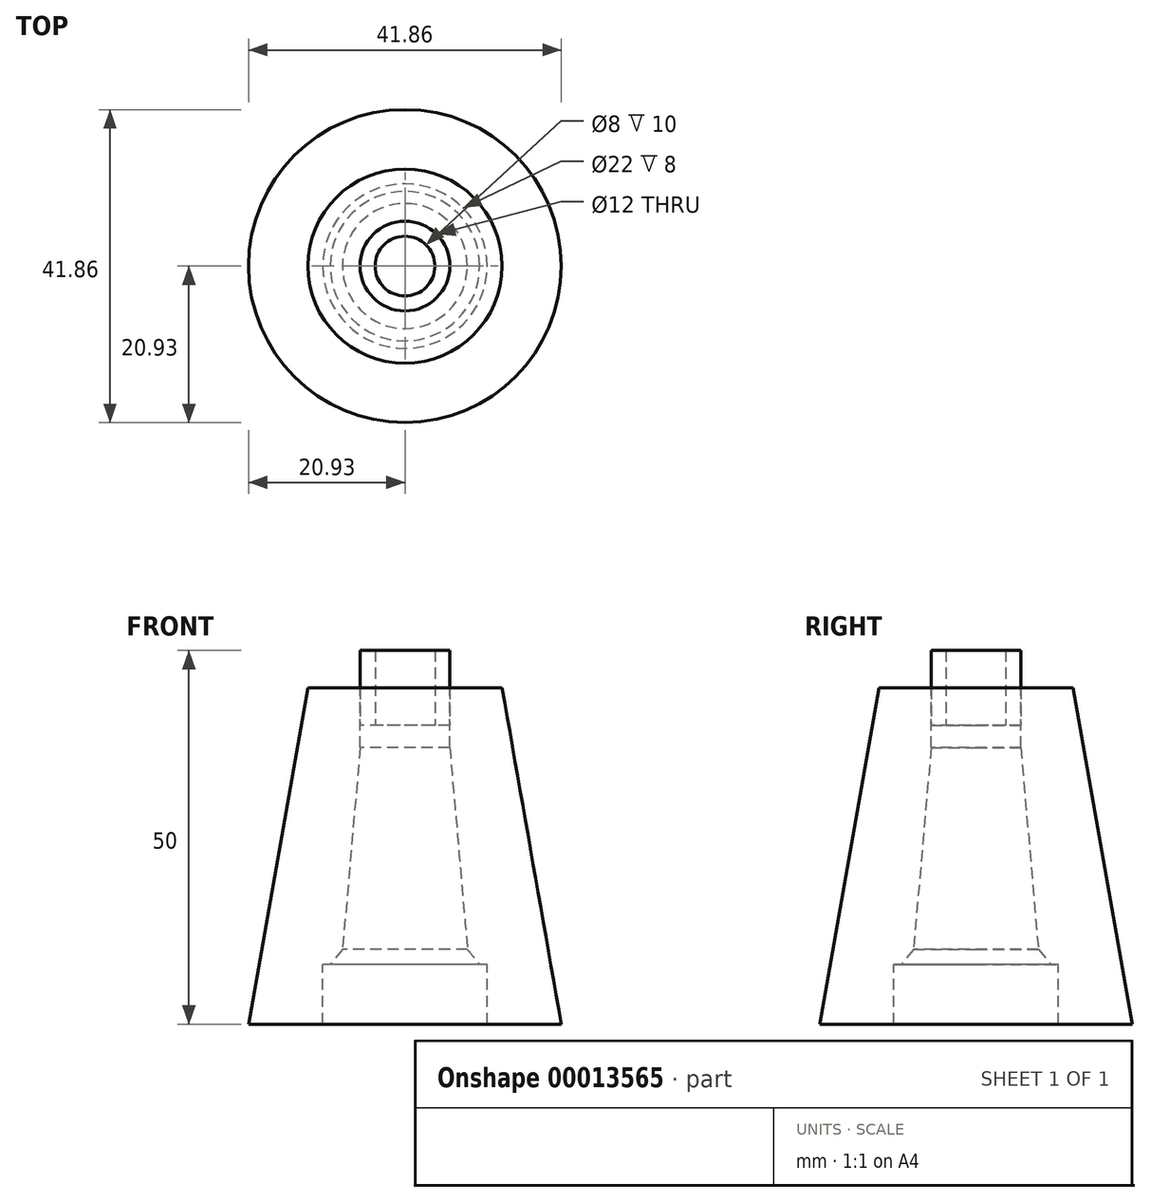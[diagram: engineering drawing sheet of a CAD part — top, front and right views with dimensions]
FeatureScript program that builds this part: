
annotation { "Feature Type Name" : "Feature", "Feature Type Description" : "" }
export const myFeature = defineFeature(function(context is Context, id is Id, definition is map)
    precondition{}
    {
        {
            var Q0;
            Q0=qCreatedBy(makeId("Front.planeOp"),FACE);
            var sketch = newSketch(context, id + "F0", { "sketchPlane" : qUnion([Q0])});
            skLineSegment(sketch, "E0", {"start": v(-10, 8) * mm, "end": v(-11, 8) * mm});
            skLineSegment(sketch, "E1", {"start": v(-11, 8) * mm, "end": v(-11, 0) * mm});
            skLineSegment(sketch, "E2", {"start": v(-11, 0) * mm, "end": v(-20.93, 0) * mm});
            skLineSegment(sketch, "E3", {"start": v(-20.93, 0) * mm, "end": v(-13, 45) * mm});
            skLineSegment(sketch, "E4", {"start": v(-8.36, 10) * mm, "end": v(-6, 37) * mm});
            skLineSegment(sketch, "E5", {"start": v(-6, 45) * mm, "end": v(-13, 45) * mm});
            skLineSegment(sketch, "E6", {"start": v(0, 54.56) * mm, "end": v(0, -18.62) * mm, "construction": true});
            skLineSegment(sketch, "E7", {"start": v(-6, 45) * mm, "end": v(-6, 37) * mm});
            skLineSegment(sketch, "E8", {"start": v(-10, 8) * mm, "end": v(-8.36, 10) * mm});
            skSolve(sketch);
        }
        {
            var Q0;
            Q0=makeQuery(id+"F0.imprint","IMPRINT",FACE,{"disambiguationData":[TD([[makeQuery(id+"F0.imprint","IMPRINT",EDGE,{"derivedFrom":sQuery(id+"F0.wireOp",EDGE,"E0")}),-1.0]])]});
            var Q1;
            Q1=sQuery(id+"F0.wireOp",EDGE,"E6");
            var Q2;
            Q2=sQuery(id+"F0.wireOp",EDGE,"E6");
            revolve(context, id + "F1", {"entities" : qUnion([Q0]), "surfaceEntities" : qUnion([Q1]), "axis" : qUnion([Q2]), "revolveType" : RevolveType.FULL});
        }
        {
            var Q0;
            Q0=makeQuery(id+"F1.opRevolve","SWEPT_FACE",FACE,{"disambiguationData":[OSD([sQuery(id+"F0.wireOp",EDGE,"E5")])]});
            var sketch = newSketch(context, id + "F2", { "sketchPlane" : qUnion([Q0])});
            skCircle(sketch, "E9", {"center": v(0, 0) * mm, "radius": 4 * mm});
            skCircle(sketch, "E10.0", {"center": v(0, 0) * mm, "radius": 6 * mm});
            skSolve(sketch);
        }
        {
            var Q0;
            Q0=makeQuery(id+"F2.imprint","IMPRINT",FACE,{"disambiguationData":[TD([[makeQuery(id+"F2.imprint","IMPRINT",EDGE,{"derivedFrom":sQuery(id+"F2.wireOp",EDGE,"E9")}),-1.0]])]});
            extrude(context, id + "F3", {"entities" : qUnion([Q0]), "endBound" : BoundingType.SYMMETRIC, "depth" : 10 * mm});
        }
    });
